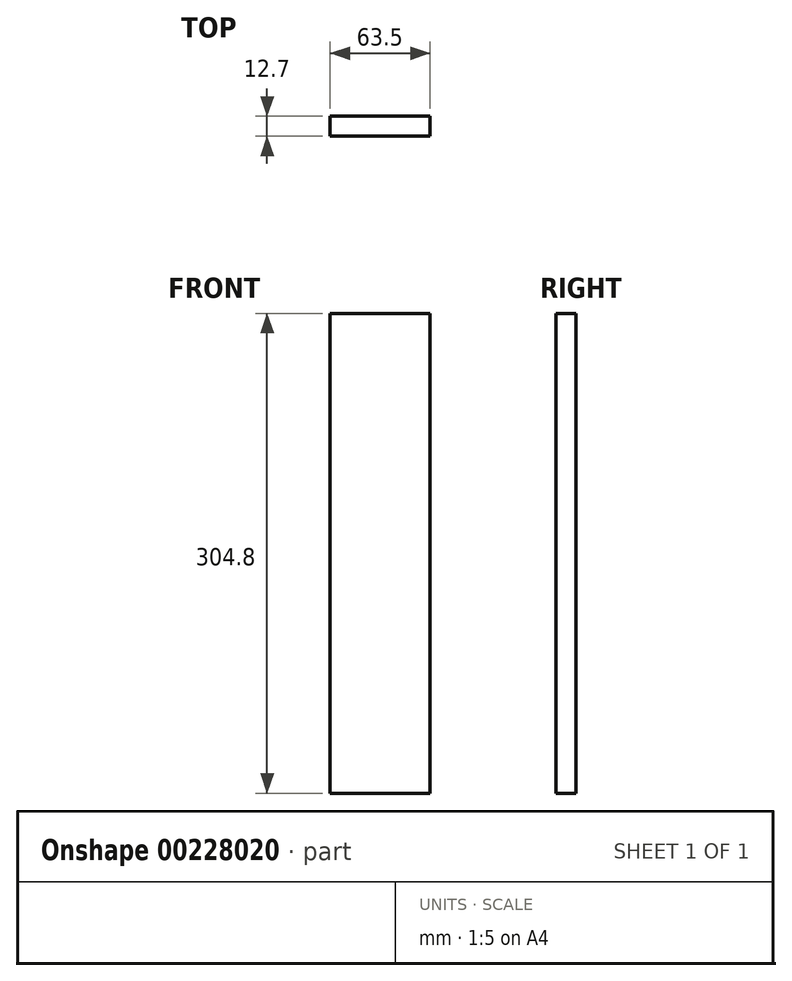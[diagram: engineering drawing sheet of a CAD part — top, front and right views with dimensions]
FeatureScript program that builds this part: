
annotation { "Feature Type Name" : "Feature", "Feature Type Description" : "" }
export const myFeature = defineFeature(function(context is Context, id is Id, definition is map)
    precondition{}
    {
        {
            var Q0;
            Q0=qCreatedBy(makeId("Front.planeOp"),FACE);
            var sketch = newSketch(context, id + "F0", { "sketchPlane" : qUnion([Q0])});
            skLineSegment(sketch, "E0.bottom", {"start": v(31.75, 152.4) * mm, "end": v(-31.75, 152.4) * mm});
            skLineSegment(sketch, "E0.top", {"start": v(31.75, -152.4) * mm, "end": v(-31.75, -152.4) * mm});
            skLineSegment(sketch, "E0.left", {"start": v(31.75, 152.4) * mm, "end": v(31.75, -152.4) * mm});
            skLineSegment(sketch, "E0.right", {"start": v(-31.75, 152.4) * mm, "end": v(-31.75, -152.4) * mm});
            skPoint(sketch, "E0.middle", {"position": v(0, 0) * mm});
            skSolve(sketch);
        }
        {
            var Q0;
            Q0=makeQuery(id+"F0.imprint","IMPRINT",FACE,{"disambiguationData":[TD([[makeQuery(id+"F0.imprint","IMPRINT",EDGE,{"derivedFrom":sQuery(id+"F0.wireOp",EDGE,"E0.bottom")}),1.0]])]});
            extrude(context, id + "F1", {"entities" : qUnion([Q0]), "depth" : 12.7 * mm});
        }
    });
